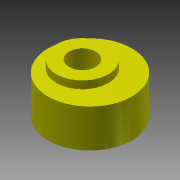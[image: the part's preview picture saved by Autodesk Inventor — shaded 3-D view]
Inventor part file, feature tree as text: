
AUTODESK INVENTOR PART (.ipt)
format: ipt  version: 2013 (Build 170138000, 138)  size: 101,888 bytes
history: native  units: mm
features: extrude x3, sketch x3
ambient origin geometry x8: Origin, YZ Plane, XZ Plane, XY Plane, X Axis, Y Axis, Z Axis, Center Point
bodies: Solid1 (feature_tree)
feature tree (6):
  extrude  "Extrusion1"  Depth=5.0mm TaperAngle=0.0deg
  extrude  "Extrusion2"  Depth=3.5mm
  extrude  "Extrusion3"  Depth=1.0mm TaperAngle=0.0deg
  sketch  "Sketch1"  dims[d0=11.0mm d3=5.0mm d4=0.0mm]
  sketch  "Sketch2"  dims[d5=1.0mm d6=3.5mm]
  sketch  "Sketch3"  dims[d7=1.666667mm d8=1.0mm d9=0.0mm d10=1.0mm d11=0.0mm]
